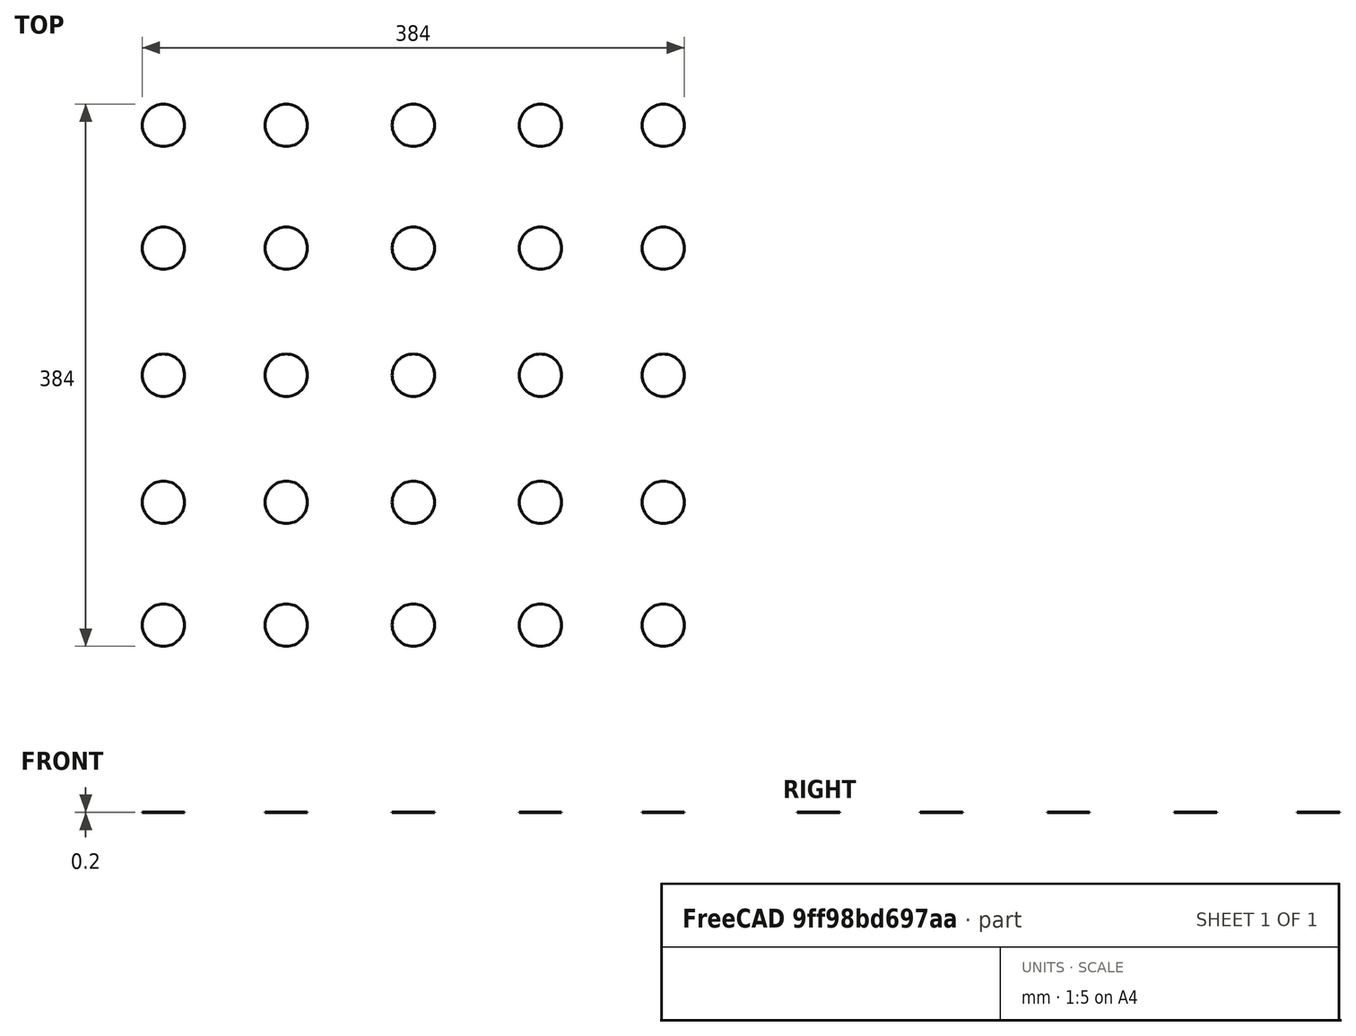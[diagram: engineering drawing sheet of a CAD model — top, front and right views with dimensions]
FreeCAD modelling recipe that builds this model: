
FCSTD DOCUMENT  (FreeCAD 0.17R13541 (Git))
Label: circle 1-25
License: All rights reserved
LicenseURL: http://en.wikipedia.org/wiki/All_rights_reserved
objects: Part::Cylinder×25
note: 25 computed .brp shape members not serialized (recipe doc carries the construction recipe); baked Part::Feature solids carry a one-line shape summary decoded from their .brp

FEATURE [Part::Cylinder] Cylinder  label="Cylinder005"
  Angle = 360
  AttacherType = Attacher::AttachEngine3D
  Height = 0.2
  Placement = pos=(382,115,0) rot=(0,0,1;0rad)
  Radius = 15
FEATURE [Part::Cylinder] Cylinder001
  Angle = 360
  AttacherType = Attacher::AttachEngine3D
  Height = 0.2
  Placement = pos=(28,115,0) rot=(0,0,1;0rad)
  Radius = 15
FEATURE [Part::Cylinder] Cylinder003
  Angle = 360
  AttacherType = Attacher::AttachEngine3D
  Height = 0.2
  Placement = pos=(205,115,0) rot=(0,0,1;0rad)
  Radius = 15
FEATURE [Part::Cylinder] Cylinder004
  Angle = 360
  AttacherType = Attacher::AttachEngine3D
  Height = 0.2
  Placement = pos=(295,115,0) rot=(0,0,1;0rad)
  Radius = 15
FEATURE [Part::Cylinder] Cylinder005  label="Cylinder006"
  Angle = 360
  AttacherType = Attacher::AttachEngine3D
  Height = 0.2
  Placement = pos=(382,205,0) rot=(0,0,1;0rad)
  Radius = 15
FEATURE [Part::Cylinder] Cylinder006  label="Cylinder007"
  Angle = 360
  AttacherType = Attacher::AttachEngine3D
  Height = 0.2
  Placement = pos=(28,205,0) rot=(0,0,1;0rad)
  Radius = 15
FEATURE [Part::Cylinder] Cylinder007  label="Cylinder008"
  Angle = 360
  AttacherType = Attacher::AttachEngine3D
  Height = 0.2
  Placement = pos=(205,205,0) rot=(0,0,1;0rad)
  Radius = 15
FEATURE [Part::Cylinder] Cylinder008  label="Cylinder009"
  Angle = 360
  AttacherType = Attacher::AttachEngine3D
  Height = 0.2
  Placement = pos=(295,205,0) rot=(0,0,1;0rad)
  Radius = 15
FEATURE [Part::Cylinder] Cylinder010  label="Cylinder014"
  Angle = 360
  AttacherType = Attacher::AttachEngine3D
  Height = 0.2
  Placement = pos=(382,295,0) rot=(0,0,1;0rad)
  Radius = 15
FEATURE [Part::Cylinder] Cylinder012  label="Cylinder013"
  Angle = 360
  AttacherType = Attacher::AttachEngine3D
  Height = 0.2
  Placement = pos=(205,295,0) rot=(0,0,1;0rad)
  Radius = 15
FEATURE [Part::Cylinder] Cylinder013  label="Cylinder011"
  Angle = 360
  AttacherType = Attacher::AttachEngine3D
  Height = 0.2
  Placement = pos=(295,295,0) rot=(0,0,1;0rad)
  Radius = 15
FEATURE [Part::Cylinder] Cylinder014  label="Cylinder012"
  Angle = 360
  AttacherType = Attacher::AttachEngine3D
  Height = 0.2
  Placement = pos=(28,295,0) rot=(0,0,1;0rad)
  Radius = 15
FEATURE [Part::Cylinder] Cylinder015  label="Cylinder019"
  Angle = 360
  AttacherType = Attacher::AttachEngine3D
  Height = 0.2
  Placement = pos=(382,382,0) rot=(0,0,1;0rad)
  Radius = 15
FEATURE [Part::Cylinder] Cylinder016  label="Cylinder020"
  Angle = 360
  AttacherType = Attacher::AttachEngine3D
  Height = 0.2
  Placement = pos=(115,115,0) rot=(0,0,1;0rad)
  Radius = 15
FEATURE [Part::Cylinder] Cylinder017  label="Cylinder016"
  Angle = 360
  AttacherType = Attacher::AttachEngine3D
  Height = 0.2
  Placement = pos=(295,382,0) rot=(0,0,1;0rad)
  Radius = 15
FEATURE [Part::Cylinder] Cylinder018  label="Cylinder017"
  Angle = 360
  AttacherType = Attacher::AttachEngine3D
  Height = 0.2
  Placement = pos=(205,382,0) rot=(0,0,1;0rad)
  Radius = 15
FEATURE [Part::Cylinder] Cylinder019  label="Cylinder018"
  Angle = 360
  AttacherType = Attacher::AttachEngine3D
  Height = 0.2
  Placement = pos=(28,382,0) rot=(0,0,1;0rad)
  Radius = 15
FEATURE [Part::Cylinder] Cylinder020  label="Cylinder023"
  Angle = 360
  AttacherType = Attacher::AttachEngine3D
  Height = 0.2
  Placement = pos=(382,28,0) rot=(0,0,1;0rad)
  Radius = 15
FEATURE [Part::Cylinder] Cylinder021  label="Cylinder024"
  Angle = 360
  AttacherType = Attacher::AttachEngine3D
  Height = 0.2
  Placement = pos=(205,28,0) rot=(0,0,1;0rad)
  Radius = 15
FEATURE [Part::Cylinder] Cylinder023  label="Cylinder021"
  Angle = 360
  AttacherType = Attacher::AttachEngine3D
  Height = 0.2
  Placement = pos=(28,28,0) rot=(0,0,1;0rad)
  Radius = 15
FEATURE [Part::Cylinder] Cylinder024  label="Cylinder022"
  Angle = 360
  AttacherType = Attacher::AttachEngine3D
  Height = 0.2
  Placement = pos=(295,28,0) rot=(0,0,1;0rad)
  Radius = 15
FEATURE [Part::Cylinder] Cylinder022  label="Cylinder025"
  Angle = 360
  AttacherType = Attacher::AttachEngine3D
  Height = 0.2
  Placement = pos=(115,382,0) rot=(0,0,1;0rad)
  Radius = 15
FEATURE [Part::Cylinder] Cylinder011  label="Cylinder015"
  Angle = 360
  AttacherType = Attacher::AttachEngine3D
  Height = 0.2
  Placement = pos=(115,295,0) rot=(0,0,1;0rad)
  Radius = 15
FEATURE [Part::Cylinder] Cylinder009  label="Cylinder010"
  Angle = 360
  AttacherType = Attacher::AttachEngine3D
  Height = 0.2
  Placement = pos=(115,205,0) rot=(0,0,1;0rad)
  Radius = 15
FEATURE [Part::Cylinder] Cylinder002
  Angle = 360
  AttacherType = Attacher::AttachEngine3D
  Height = 0.2
  Placement = pos=(115,28,0) rot=(0,0,1;0rad)
  Radius = 15
